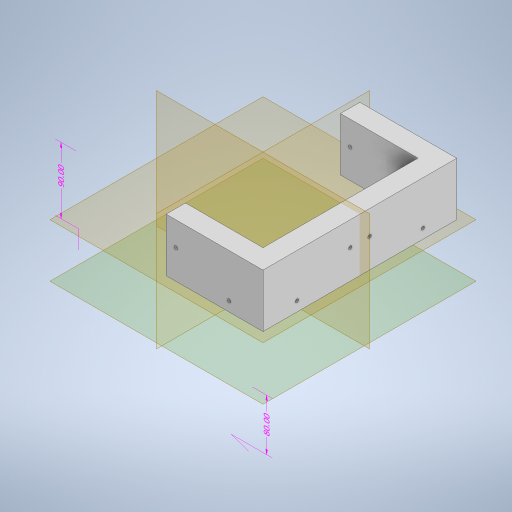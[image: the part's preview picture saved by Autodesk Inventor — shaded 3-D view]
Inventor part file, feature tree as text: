
AUTODESK INVENTOR PART (.ipt)
format: ipt  version: 2023 (Build 270158000, 158)  size: 425,472 bytes
history: native  units: mm
features: sketch x9, extrude x5, other x4, hole x4, plane x4, split x3
ambient origin geometry x8: Origin, YZ Plane, XZ Plane, XY Plane, X Axis, Y Axis, Z Axis, Center Point
bodies: Body1 (feature_tree)
feature tree (29):
  other  "Sólido1"
  other  "Anotaciones"
  extrude  "Extrusión1"  Depth=200.0mm
  hole  "Agujero1"  [1 undecoded]
  extrude  "Extrusión2"  Depth=15.0mm
  extrude  "Extrusión3"  Depth=80.0mm TaperAngle=0.0deg
  extrude  "Extrusión4"  Depth=200.0mm
  extrude  "Extrusión5"  Depth=20.0mm
  hole  "Agujero2"  [1 undecoded]
  plane  "Plano de trabajo1"
  split  "Dividir1"
  plane  "Plano de trabajo2"
  plane  "Plano de trabajo3"
  sketch  "Boceto9"  dims[d37=20.0mm d38=20.0mm]
  plane  "Plano de trabajo4"
  hole  "Agujero3"  [1 undecoded]
  hole  "Agujero4"  [1 undecoded]
  split  "Dividir2"
  split  "Dividir3"
  sketch  "Boceto2"  dims[d7=15.0mm d8=200.0mm]
  sketch  "Boceto3"  dims[d9=10.0mm d10=0.0mm]
  sketch  "Boceto4"  dims[d12=1.75mm d13=1.75mm d14=1.75mm d15=1.75mm d16=10.0mm d17=10.0mm d19=30.0mm]
  sketch  "Boceto5"  dims[d20=3.5mm d21=6.0mm d22=4.0mm d23=2.0mm d24=90.0deg d25=8.0mm d26=20.594885mm d27=15.0mm]
  sketch  "Boceto6"  dims[d28=20.0mm d29=80.0mm d30=0.0mm]
  sketch  "Boceto7"  dims[d31=48.0mm d32=200.0mm]
  sketch  "Boceto8"  dims[d33=110.0mm d34=0.0mm d36=20.0mm]
  sketch  "Boceto10"  dims[d39=90.0mm d40=0.0mm d42=10.0mm d43=30.0mm d44=0.0mm d46=1.75mm d47=1.75mm d48=1.75mm d49=1.75mm d50=10.0mm d51=10.0mm d52=15.0mm d56=3.5mm d57=6.0mm d58=4.0mm d59=2.0mm d60=90.0deg d61=8.0mm d62=20.594885mm d63=10.0mm d65=10.0mm d66=10.0mm d67=31.75mm d70=15.0mm d74=200.0mm d78=20.0mm d82=90.0deg d83=10.0mm d84=30.0mm d85=5.0mm d86=5.0mm d87=5.0mm d88=5.0mm d89=20.0mm d91=30.0mm d92=5.0mm d93=5.0mm d94=3.5mm d95=5.0mm d96=5.0mm d97=5.0mm d98=5.0mm d99=5.0mm d100=20.0mm d101=3.5mm d102=6.0mm d103=4.0mm d104=2.0mm d105=90.0deg d106=8.0mm d107=20.594885mm d108=10.0mm d109=30.0mm d110=5.0mm d111=5.0mm d112=5.0mm d113=5.0mm d114=5.0mm d115=5.0mm d116=3.5mm d117=5.0mm d118=5.0mm d119=5.0mm d120=5.0mm d121=5.0mm d122=30.0mm d123=30.0mm d124=3.5mm d125=6.0mm d126=4.0mm d127=2.0mm d128=90.0deg d129=8.0mm d130=20.594885mm d75=1.454734mm d76=6.982969mm d77=80.0mm d79=4.097996mm d80=1.406125mm d81=90.0mm]
  other  "Cota lineal 2"
  other  "Cota lineal 3"
note: 4 required parameter values undecoded (feature->parameter linkage not recoverable at this tier; creation-order binding heuristic only, values carry confidence <= 0.55)
